# Revit family: NBS_wediSystemsUKLtd_ShwrTrys_wediFundoBorgo
name_source: partatom
category: Plumbing Fixtures
units: mm (PartAtom-declared; Revit-internal decimal feet)

## family parameters
Cut with Voids When Loaded = No
Host = Face
Part Type = Normal
Room Calculation Point = No
Round Connector Dimension = Use Diameter
Shared = No

## types (3) — shared parameters
AssetType = Fixed
Category = Pr_40_20_06_84:Shower trays
Color = Grey
CompressiveStrength = 0.08 N/mm²
Default Elevation = 1219 mm
Density = 32 kg/m³
Description = wedi Fundo Borgo, floor element, Complete system incl. drainage technology, point drain
DurationUnit = year
ExpectedLife = 30
Finish = resistant and glass fibre reinforced cement coating
FirePerformance = Class E
Form = Floor-level shower element for direct tiling with horizontal floor drain, Minimal installation height of 65 mm incl. Drain
IfcExportAs = IfcSanitaryTerminalType
IfcExportType = SHOWER
Length = 900 mm  [stored 2.95276 ft]
ManufacturerName = wedi Systems (UK) Ltd
ManufacturerURL = https://www.wedi.de
Material = A waterproof extruded polystyrene rigid foam core with a special, resistant and glass fibre reinforced cement coating
MaterialsBody = A waterproof extruded polystyrene rigid foam core with a special, resistant and glass fibre reinforced cement coating
ModelReference = wedi Fundo Borgo floor element
NBSCertification = www.nationalbimlibrary.com/cert/qj1xjcpp
NBSDescription = Shower trays
NBSReference = 45-35-70/336
NominalHeight = 40 mm
NominalLength = 900 mm  [stored 2.95276 ft]
NominalWidth = 900 mm  [stored 2.95276 ft]
OperatingTemperatureRange = -50°C / +75°C
ProductInformation = https://www.wedi.de
Shape = Square
ThermalConductivity = 0.036 W/mK
Uniclass2015Code = Pr_40_20_06_84
Uniclass2015Title = Shower trays
Uniclass2015Version = Products v1.14
Version = 1
WarrantyDescription = available on request
WarrantyDurationUnit = year
WasteHole = DN40
WediStructuralMaterial = NBS_wedi_PolystyreneExpanded
Width = 900 mm  [stored 2.95276 ft]

## per-type parameters (varying)
| type | BIMObjectName | FaceFinish | Features | ModelNumber | Name | Size |
| wedi Fundo Borgo floor element | NBS_wediSystemsUKLtd_ShowerTrays_wediFundoBorgo_900x900x40mm | <By Category> | Minimal installation height of 65 mm incl, Drain, Ideally suited for renovations, Precise slope with integrated drain, 100% waterproof to the core | 073735576 | ShowerTrays_wediFundoBorgo_900x900x40mm_wediSystemsUKLtd | 900 x 900 x 40 mm |
| wediFundoBorgo_900x900x40mm | NBS_wediSystemsUKLtd_ShowerTrays_wediFundoBorgo_900x900x40mm | <By Category> | Minimal installation height of 65 mm incl. Drain, Ideally suited for renovations, Precise slope with integrated drain, 100% waterproof to the core | 073735576 | ShowerTrays_wediFundoBorgo_900x900x40mm_wediSystemsUKLtd | 900 x 900 x 40 mm |
| wediFundoBorgo_1000x1000x40mm | NBS_wediSystemsUKLtd_ShowerTrays_wediFundoBorgo_1000x1000x40mm | NBS_wedi_PolystyreneExpanded | Minimal installation height of 65 mm incl. Drain, Ideally suited for renovations, Precise slope with integrated drain, 100% waterproof to the core | 073736576 | ShowerTrays_wediFundoBorgo_1000x1000x40mm_wediSystemsUKLtd | 1000 x 1000 x 40 mm |

note: [stored X ft] marks values corroborated as IEEE doubles in the binary element streams (Revit-internal decimal feet)

## geometry (parser evidence)
native form markers: Sweep x3
no freeform markers — native parametric forms only
